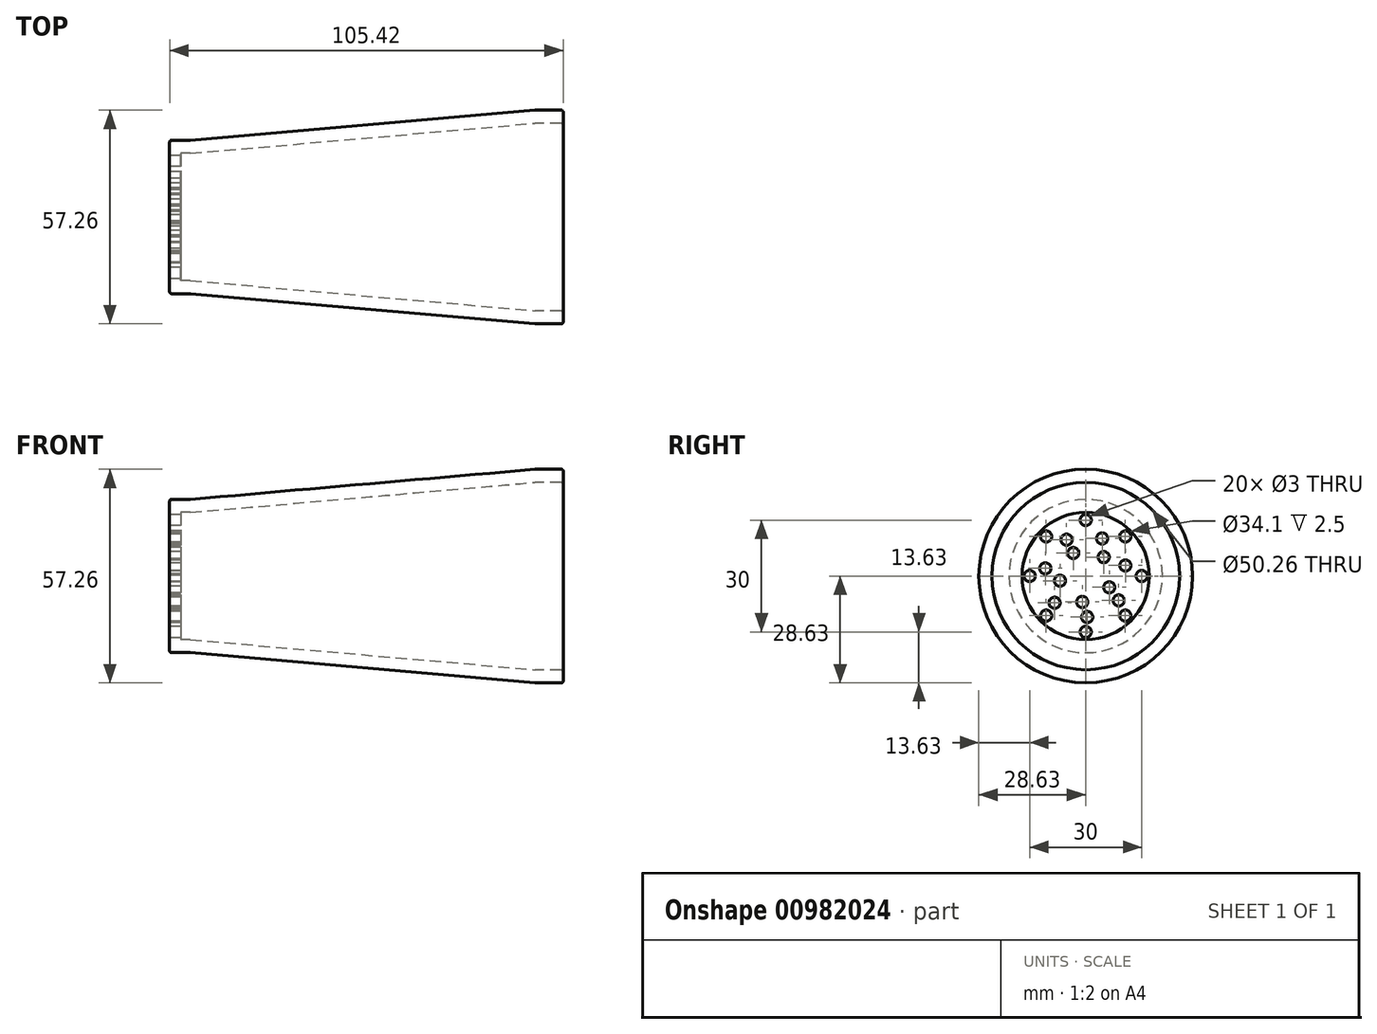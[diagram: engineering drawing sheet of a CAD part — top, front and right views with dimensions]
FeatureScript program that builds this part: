
annotation { "Feature Type Name" : "Feature", "Feature Type Description" : "" }
export const myFeature = defineFeature(function(context is Context, id is Id, definition is map)
    precondition{}
    {
        {
            var Q0;
            Q0=qCreatedBy(makeId("Front.planeOp"),FACE);
            var sketch = newSketch(context, id + "F0", { "sketchPlane" : qUnion([Q0])});
            skLineSegment(sketch, "E0", {"start": v(-105.65, 0) * mm, "end": v(152.13, 0) * mm, "construction": true});
            skLineSegment(sketch, "E1", {"start": v(-16.93, 17.55) * mm, "end": v(-16.93, 20.05) * mm});
            skLineSegment(sketch, "E2", {"start": v(-16.43, 20.55) * mm, "end": v(-11.43, 20.55) * mm});
            skLineSegment(sketch, "E3", {"start": v(-11.39, 20.55) * mm, "end": v(80.95, 28.63) * mm});
            skLineSegment(sketch, "E4", {"start": v(81, 28.63) * mm, "end": v(88, 28.63) * mm});
            skLineSegment(sketch, "E5", {"start": v(88.5, 28.13) * mm, "end": v(88.5, 25.63) * mm});
            skLineSegment(sketch, "E6", {"start": v(88, 25.13) * mm, "end": v(81, 25.13) * mm});
            skLineSegment(sketch, "E7", {"start": v(80.95, 25.13) * mm, "end": v(-11.39, 17.05) * mm});
            skPoint(sketch, "E8.visualSharp", {"position": v(-16.93, 14.85) * mm});
            skPoint(sketch, "E9.visualSharp", {"position": v(-11.41, 20.55) * mm});
            skArc(sketch, "E9.filletArc", {"start": v(-11.43, 20.55) * mm, "mid": v(-11.41, 20.55) * mm, "end": v(-11.39, 20.55) * mm});
            skPoint(sketch, "E10.visualSharp", {"position": v(-11.41, 17.05) * mm});
            skArc(sketch, "E10.filletArc", {"start": v(-11.43, 17.05) * mm, "mid": v(-11.41, 17.05) * mm, "end": v(-11.39, 17.05) * mm});
            skPoint(sketch, "E11.visualSharp", {"position": v(-16.93, 20.55) * mm});
            skArc(sketch, "E11.filletArc", {"start": v(-16.43, 20.55) * mm, "mid": v(-16.79, 20.4) * mm, "end": v(-16.93, 20.05) * mm});
            skPoint(sketch, "E12.visualSharp", {"position": v(80.97, 25.13) * mm});
            skArc(sketch, "E12.filletArc", {"start": v(81, 25.13) * mm, "mid": v(80.97, 25.13) * mm, "end": v(80.95, 25.13) * mm});
            skPoint(sketch, "E13.visualSharp", {"position": v(88.5, 25.13) * mm});
            skArc(sketch, "E13.filletArc", {"start": v(88, 25.13) * mm, "mid": v(88.34, 25.28) * mm, "end": v(88.5, 25.63) * mm});
            skPoint(sketch, "E14.visualSharp", {"position": v(88.5, 28.63) * mm});
            skArc(sketch, "E14.filletArc", {"start": v(88.5, 28.13) * mm, "mid": v(88.34, 28.48) * mm, "end": v(88, 28.63) * mm});
            skPoint(sketch, "E15.visualSharp", {"position": v(80.97, 28.63) * mm});
            skArc(sketch, "E15.filletArc", {"start": v(81, 28.63) * mm, "mid": v(80.97, 28.63) * mm, "end": v(80.95, 28.63) * mm});
            skLineSegment(sketch, "E16", {"start": v(-16.93, 14.85) * mm, "end": v(-16.93, 0) * mm});
            skLineSegment(sketch, "E17", {"start": v(-16.93, 0) * mm, "end": v(-13.93, 0) * mm});
            skPoint(sketch, "E17.endSnap0", {"position": v(-13.93, 17.05) * mm});
            skLineSegment(sketch, "E18", {"start": v(-13.93, 0) * mm, "end": v(-13.93, 17.05) * mm});
            skLineSegment(sketch, "E19", {"start": v(-16.93, 17.55) * mm, "end": v(-16.93, 14.85) * mm});
            skLineSegment(sketch, "E20", {"start": v(-13.93, 17.05) * mm, "end": v(-11.43, 17.05) * mm});
            skSolve(sketch);
        }
        {
            var Q0;
            Q0=makeQuery(id+"F0.imprint","IMPRINT",FACE,{"disambiguationData":[TD([[makeQuery(id+"F0.imprint","IMPRINT",EDGE,{"derivedFrom":sQuery(id+"F0.wireOp",EDGE,"E1")}),-1.0]])]});
            var Q1;
            Q1=sQuery(id+"F0.wireOp",EDGE,"E0");
            revolve(context, id + "F1", {"surfaceOperationType" : NewSurfaceOperationType.NEW, "entities" : qUnion([Q0]), "axis" : qUnion([Q1]), "revolveType" : RevolveType.FULL});
        }
        {
            var Q0;
            Q0=makeQuery(id+"F1.opRevolve","SWEPT_FACE",FACE,{"disambiguationData":[OSD([sQuery(id+"F0.wireOp",EDGE,"E1"),sQuery(id+"F0.wireOp",EDGE,"E16"),sQuery(id+"F0.wireOp",EDGE,"E19")])]});
            var sketch = newSketch(context, id + "F2", { "sketchPlane" : qUnion([Q0])});
            skCircle(sketch, "E21", {"center": v(0, 0) * mm, "radius": 15 * mm, "construction": true});
            skCircle(sketch, "E22", {"center": v(0, 0) * mm, "radius": 11 * mm, "construction": true});
            skCircle(sketch, "E23", {"center": v(0, 0) * mm, "radius": 7 * mm, "construction": true});
            skCircle(sketch, "E24", {"center": v(0, 15) * mm, "radius": 1.5 * mm});
            skCircle(sketch, "E25.1.0", {"center": v(-10.6, 10.6) * mm, "radius": 1.5 * mm});
            skCircle(sketch, "E25.2.0", {"center": v(-15, 0) * mm, "radius": 1.5 * mm});
            skCircle(sketch, "E25.3.0", {"center": v(-10.6, -10.6) * mm, "radius": 1.5 * mm});
            skCircle(sketch, "E25.4.0", {"center": v(0, -15) * mm, "radius": 1.5 * mm});
            skCircle(sketch, "E25.5.0", {"center": v(10.6, -10.6) * mm, "radius": 1.5 * mm});
            skCircle(sketch, "E25.6.0", {"center": v(15, 0) * mm, "radius": 1.5 * mm});
            skCircle(sketch, "E25.7.0", {"center": v(10.6, 10.6) * mm, "radius": 1.5 * mm});
            skCircle(sketch, "E26", {"center": v(-4.4, 10.08) * mm, "radius": 1.5 * mm});
            skCircle(sketch, "E27.1.0", {"center": v(-10.63, 2.84) * mm, "radius": 1.5 * mm});
            skCircle(sketch, "E27.2.0", {"center": v(-8.84, -6.54) * mm, "radius": 1.5 * mm});
            skCircle(sketch, "E27.3.0", {"center": v(-0.4, -11) * mm, "radius": 1.5 * mm});
            skCircle(sketch, "E27.4.0", {"center": v(8.34, -7.17) * mm, "radius": 1.5 * mm});
            skCircle(sketch, "E27.5.0", {"center": v(10.8, 2.05) * mm, "radius": 1.5 * mm});
            skCircle(sketch, "E27.6.0", {"center": v(5.13, 9.73) * mm, "radius": 1.5 * mm});
            skCircle(sketch, "E28", {"center": v(-4.83, 5.07) * mm, "radius": 1.5 * mm});
            skCircle(sketch, "E29.1.0", {"center": v(-6.31, -3.03) * mm, "radius": 1.5 * mm});
            skCircle(sketch, "E29.2.0", {"center": v(0.93, -6.94) * mm, "radius": 1.5 * mm});
            skCircle(sketch, "E29.3.0", {"center": v(6.89, -1.26) * mm, "radius": 1.5 * mm});
            skCircle(sketch, "E29.4.0", {"center": v(3.33, 6.16) * mm, "radius": 1.5 * mm});
            skSolve(sketch);
        }
        {
            var Q0;
            Q0 = qSketchRegion(id + "F2", true);
            extrude(context, id + "F3", {"entities" : qUnion([Q0]), "operationType" : NewBodyOperationType.REMOVE, "oppositeDirection" : true, "depth" : 25 * mm, "offsetDistance" : 25 * mm});
        }
    });
